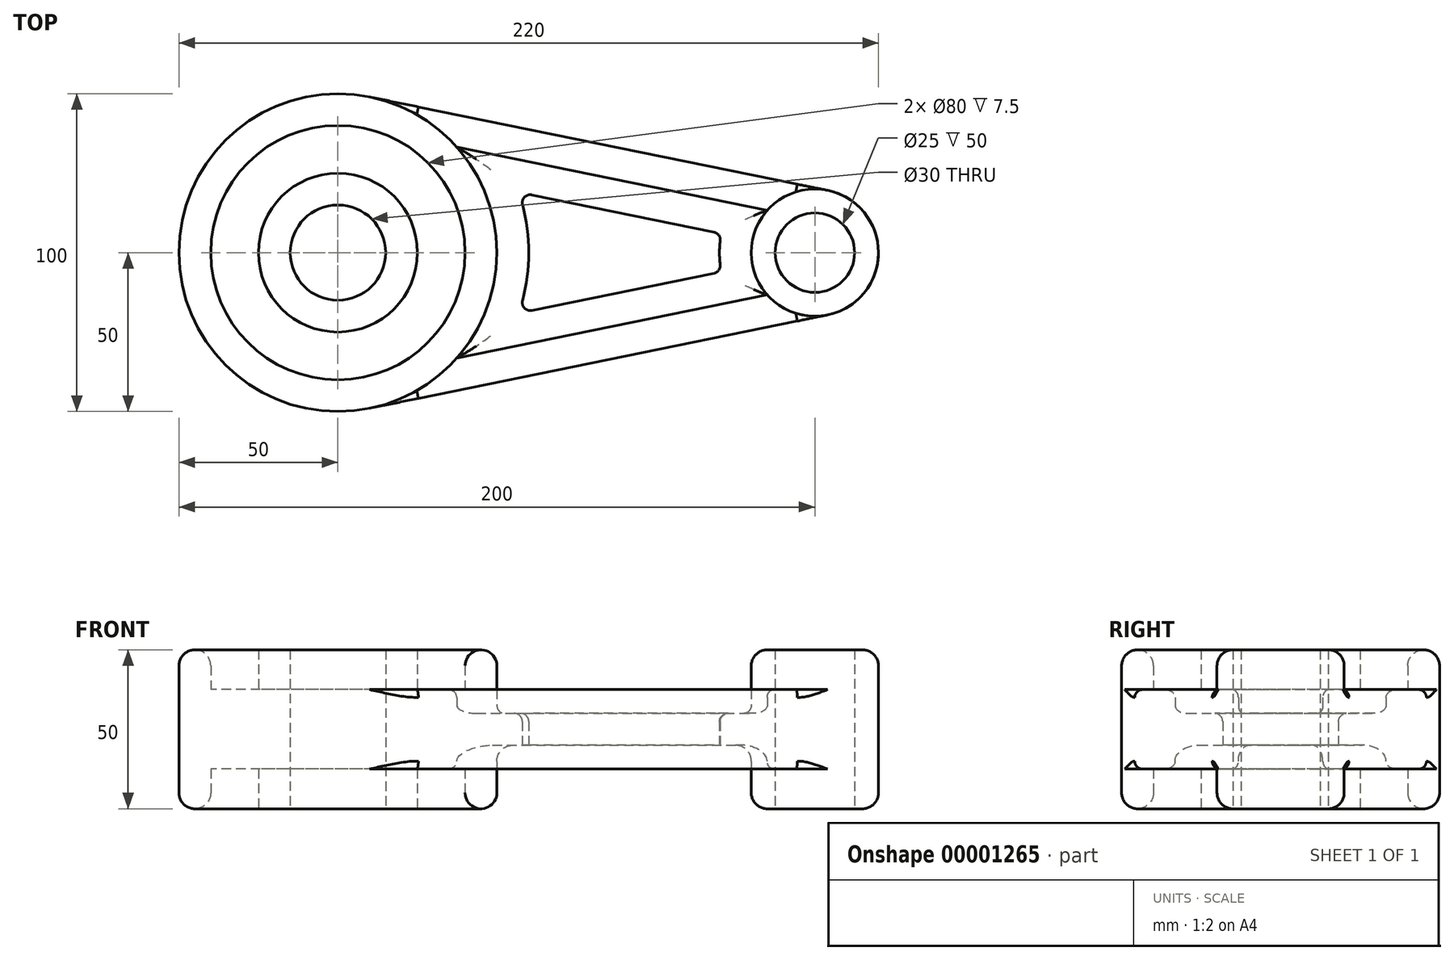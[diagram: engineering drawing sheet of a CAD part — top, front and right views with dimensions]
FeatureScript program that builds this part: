
annotation { "Feature Type Name" : "Feature", "Feature Type Description" : "" }
export const myFeature = defineFeature(function(context is Context, id is Id, definition is map)
    precondition{}
    {
        {
            var Q0;
            Q0=qCreatedBy(makeId("Top.planeOp"),FACE);
            var sketch = newSketch(context, id + "F0", { "sketchPlane" : qUnion([Q0])});
            skCircle(sketch, "E0", {"center": v(150, 0) * mm, "radius": 12.5 * mm});
            skCircle(sketch, "E1", {"center": v(150, 0) * mm, "radius": 20 * mm});
            skCircle(sketch, "E2", {"center": v(0, 0) * mm, "radius": 15 * mm});
            skCircle(sketch, "E3", {"center": v(0, 0) * mm, "radius": 50 * mm});
            skLineSegment(sketch, "E4", {"start": v(10, 48.99) * mm, "end": v(154, 19.6) * mm});
            skLineSegment(sketch, "E5", {"start": v(10, -48.99) * mm, "end": v(154, -19.6) * mm});
            skCircle(sketch, "E6", {"center": v(0, 0) * mm, "radius": 25 * mm});
            skCircle(sketch, "E7", {"center": v(0, 0) * mm, "radius": 40 * mm});
            skLineSegment(sketch, "E8.0", {"start": v(37.4, 33.2) * mm, "end": v(135.03, 13.26) * mm});
            skLineSegment(sketch, "E9.0", {"start": v(37.4, -33.2) * mm, "end": v(135.03, -13.26) * mm});
            skLineSegment(sketch, "E10", {"start": v(0, 0) * mm, "end": v(150, 0) * mm, "construction": true});
            skSolve(sketch);
        }
        {
            var Q0;
            Q0=makeQuery(id+"F0.imprint","IMPRINT",FACE,{"disambiguationData":[TD([[makeQuery(id+"F0.imprint","IMPRINT",EDGE,{"derivedFrom":sQuery(id+"F0.wireOp",EDGE,"E2")}),-1.0]])]});
            var Q1;
            Q1=makeQuery(id+"F0.imprint","IMPRINT",FACE,{"disambiguationData":[TD([[makeQuery(id+"F0.imprint","IMPRINT",EDGE,{"derivedFrom":sQuery(id+"F0.wireOp",EDGE,"E7")}),-1.0]])]});
            var Q2;
            Q2=makeQuery(id+"F0.imprint","IMPRINT",FACE,{"disambiguationData":[TD([[makeQuery(id+"F0.imprint","IMPRINT",EDGE,{"derivedFrom":sQuery(id+"F0.wireOp",EDGE,"E0")}),-1.0]])]});
            extrude(context, id + "F1", {"entities" : qUnion([Q0, Q1, Q2]), "depth" : 50 * mm, "symmetric" : true});
        }
        {
            var Q0;
            Q0=makeQuery(id+"F0.imprint","IMPRINT",FACE,{"disambiguationData":[TD([[makeQuery(id+"F0.imprint","IMPRINT",EDGE,{"derivedFrom":sQuery(id+"F0.wireOp",EDGE,"E6")}),-1.0]])]});
            var Q1;
            {var subQ0=sQuery(id+"F0.wireOp",EDGE,"E4");Q1=makeQuery(id+"F0.imprint","IMPRINT",FACE,{"disambiguationData":[TD([[makeQuery(id+"F0.imprint","IMPRINT",EDGE,{"derivedFrom":subQ0}),-1.0]])]});}
            var Q2;
            {var subQ0=sQuery(id+"F0.wireOp",EDGE,"E5");Q2=makeQuery(id+"F0.imprint","IMPRINT",FACE,{"disambiguationData":[TD([[makeQuery(id+"F0.imprint","IMPRINT",EDGE,{"derivedFrom":subQ0}),1.0]])]});}
            extrude(context, id + "F2", {"entities" : qUnion([Q0, Q1, Q2]), "operationType" : NewBodyOperationType.ADD, "depth" : 25 * mm, "symmetric" : true});
        }
        {
            var Q0;
            {var subQ0=sQuery(id+"F0.wireOp",EDGE,"E8.0");Q0=makeQuery(id+"F0.imprint","IMPRINT",FACE,{"disambiguationData":[TD([[makeQuery(id+"F0.imprint","IMPRINT",EDGE,{"derivedFrom":subQ0}),-1.0]])]});}
            extrude(context, id + "F3", {"entities" : qUnion([Q0]), "operationType" : NewBodyOperationType.ADD, "depth" : 10 * mm, "symmetric" : true});
        }
        {
            var Q0;
            Q0=makeQuery(id+"F2.opExtrude","CAP_EDGE",EDGE,{"disambiguationData":[OSD([sQuery(id+"F0.wireOp",EDGE,"E3")])],"isStart":false});
            var Q1;
            Q1=makeQuery(id+"F2.opExtrude","CAP_EDGE",EDGE,{"disambiguationData":[OSD([sQuery(id+"F0.wireOp",EDGE,"E6")])],"isStart":false});
            var Q2;
            Q2=makeQuery(id+"F2.opExtrude","CAP_EDGE",EDGE,{"disambiguationData":[OSD([sQuery(id+"F0.wireOp",EDGE,"E7")])],"isStart":false});
            var Q3;
            Q3=makeQuery(id+"F2.opExtrude","CAP_EDGE",EDGE,{"disambiguationData":[OSD([sQuery(id+"F0.wireOp",EDGE,"E3")])],"isStart":true});
            var Q4;
            Q4=makeQuery(id+"F2.opExtrude","CAP_EDGE",EDGE,{"disambiguationData":[OSD([sQuery(id+"F0.wireOp",EDGE,"E7")])],"isStart":true});
            var Q5;
            Q5=makeQuery(id+"F2.opExtrude","CAP_EDGE",EDGE,{"disambiguationData":[OSD([sQuery(id+"F0.wireOp",EDGE,"E6")])],"isStart":true});
            var Q6;
            Q6=makeQuery(id+"F2.opExtrude","CAP_EDGE",EDGE,{"disambiguationData":[OSD([sQuery(id+"F0.wireOp",EDGE,"E1")])],"isStart":true});
            var Q7;
            Q7=makeQuery(id+"F2.opExtrude","CAP_EDGE",EDGE,{"disambiguationData":[OSD([sQuery(id+"F0.wireOp",EDGE,"E1")])],"isStart":false});
            var Q8;
            Q8=makeQuery(id+"F3.opExtrude","CAP_EDGE",EDGE,{"disambiguationData":[OSD([sQuery(id+"F0.wireOp",EDGE,"E8.0")])],"isStart":false});
            var Q9;
            Q9=makeQuery(id+"F3.opExtrude","CAP_EDGE",EDGE,{"disambiguationData":[OSD([sQuery(id+"F0.wireOp",EDGE,"E3")])],"isStart":false});
            var Q10;
            Q10=makeQuery(id+"F3.opExtrude","CAP_EDGE",EDGE,{"disambiguationData":[OSD([sQuery(id+"F0.wireOp",EDGE,"E9.0")])],"isStart":false});
            var Q11;
            Q11=makeQuery(id+"F3.opExtrude","CAP_EDGE",EDGE,{"disambiguationData":[OSD([sQuery(id+"F0.wireOp",EDGE,"E1")])],"isStart":false});
            var Q12;
            {var subQ0=sQuery(id+"F0.wireOp",EDGE,"E1");var subQ1=sQuery(id+"F0.wireOp",EDGE,"E8.0");var subQ2=sQuery(id+"F0.wireOp",EDGE,"E3");Q12=makeQuery(id+"F3.boolean.opBoolean","SPLIT",EDGE,{"disambiguationData":[TD([makeQuery(id+"F2.opExtrude","CAP_FACE",FACE,{"disambiguationData":[OSD([subQ0,subQ2,sQuery(id+"F0.wireOp",EDGE,"E4"),subQ1])],"isStart":false})])],"derivedFrom":makeQuery(id+"F2.opExtrude","SWEPT_EDGE",EDGE,{"disambiguationData":[OSD([subQ0,subQ1])]})});}
            var Q13;
            {var subQ0=sQuery(id+"F0.wireOp",EDGE,"E1");var subQ1=sQuery(id+"F0.wireOp",EDGE,"E9.0");var subQ2=sQuery(id+"F0.wireOp",EDGE,"E3");Q13=makeQuery(id+"F3.boolean.opBoolean","SPLIT",EDGE,{"disambiguationData":[TD([makeQuery(id+"F2.opExtrude","CAP_FACE",FACE,{"disambiguationData":[OSD([subQ0,subQ2,sQuery(id+"F0.wireOp",EDGE,"E5"),subQ1])],"isStart":false})])],"derivedFrom":makeQuery(id+"F2.opExtrude","SWEPT_EDGE",EDGE,{"disambiguationData":[OSD([subQ0,subQ1])]})});}
            var Q14;
            Q14=makeQuery(id+"F3.opExtrude","CAP_EDGE",EDGE,{"disambiguationData":[OSD([sQuery(id+"F0.wireOp",EDGE,"E3")])],"isStart":true});
            var Q15;
            Q15=makeQuery(id+"F3.opExtrude","CAP_EDGE",EDGE,{"disambiguationData":[OSD([sQuery(id+"F0.wireOp",EDGE,"E9.0")])],"isStart":true});
            var Q16;
            Q16=makeQuery(id+"F3.opExtrude","CAP_EDGE",EDGE,{"disambiguationData":[OSD([sQuery(id+"F0.wireOp",EDGE,"E8.0")])],"isStart":true});
            var Q17;
            Q17=makeQuery(id+"F3.opExtrude","CAP_FACE",FACE,{"disambiguationData":[OSD([sQuery(id+"F0.wireOp",EDGE,"E1"),sQuery(id+"F0.wireOp",EDGE,"E3"),sQuery(id+"F0.wireOp",EDGE,"E8.0"),sQuery(id+"F0.wireOp",EDGE,"E9.0")])],"isStart":true});
            var Q18;
            {var subQ0=sQuery(id+"F0.wireOp",EDGE,"E1");var subQ1=sQuery(id+"F0.wireOp",EDGE,"E8.0");var subQ2=sQuery(id+"F0.wireOp",EDGE,"E3");Q18=makeQuery(id+"F3.boolean.opBoolean","SPLIT",EDGE,{"disambiguationData":[TD([makeQuery(id+"F2.opExtrude","CAP_FACE",FACE,{"disambiguationData":[OSD([subQ0,subQ2,sQuery(id+"F0.wireOp",EDGE,"E4"),subQ1])],"isStart":true})])],"derivedFrom":makeQuery(id+"F2.opExtrude","SWEPT_EDGE",EDGE,{"disambiguationData":[OSD([subQ0,subQ1])]})});}
            var Q19;
            {var subQ0=sQuery(id+"F0.wireOp",EDGE,"E1");var subQ1=sQuery(id+"F0.wireOp",EDGE,"E9.0");var subQ2=sQuery(id+"F0.wireOp",EDGE,"E3");Q19=makeQuery(id+"F3.boolean.opBoolean","SPLIT",EDGE,{"disambiguationData":[TD([makeQuery(id+"F2.opExtrude","CAP_FACE",FACE,{"disambiguationData":[OSD([subQ0,subQ2,sQuery(id+"F0.wireOp",EDGE,"E5"),subQ1])],"isStart":true})])],"derivedFrom":makeQuery(id+"F2.opExtrude","SWEPT_EDGE",EDGE,{"disambiguationData":[OSD([subQ0,subQ1])]})});}
            var Q20;
            Q20=makeQuery(id+"F1.opExtrude","CAP_EDGE",EDGE,{"disambiguationData":[OSD([sQuery(id+"F0.wireOp",EDGE,"E1")])],"isStart":true});
            var Q21;
            Q21=makeQuery(id+"F1.opExtrude","CAP_EDGE",EDGE,{"disambiguationData":[OSD([sQuery(id+"F0.wireOp",EDGE,"E1")])],"isStart":false});
            var Q22;
            Q22=makeQuery(id+"F1.opExtrude","CAP_EDGE",EDGE,{"disambiguationData":[OSD([sQuery(id+"F0.wireOp",EDGE,"E3")])],"isStart":true});
            var Q23;
            Q23=makeQuery(id+"F1.opExtrude","CAP_EDGE",EDGE,{"disambiguationData":[OSD([sQuery(id+"F0.wireOp",EDGE,"E3")])],"isStart":false});
            var Q24;
            {var subQ0=sQuery(id+"F0.wireOp",EDGE,"E3");var subQ1=sQuery(id+"F0.wireOp",EDGE,"E8.0");var subQ2=sQuery(id+"F0.wireOp",EDGE,"E1");Q24=makeQuery(id+"F3.boolean.opBoolean","SPLIT",EDGE,{"disambiguationData":[TD([makeQuery(id+"F2.opExtrude","CAP_FACE",FACE,{"disambiguationData":[OSD([subQ2,subQ0,sQuery(id+"F0.wireOp",EDGE,"E4"),subQ1])],"isStart":false})])],"derivedFrom":makeQuery(id+"F2.opExtrude","SWEPT_EDGE",EDGE,{"disambiguationData":[OSD([subQ0,subQ1])]})});}
            var Q25;
            {var subQ0=sQuery(id+"F0.wireOp",EDGE,"E3");var subQ1=sQuery(id+"F0.wireOp",EDGE,"E9.0");var subQ2=sQuery(id+"F0.wireOp",EDGE,"E1");Q25=makeQuery(id+"F3.boolean.opBoolean","SPLIT",EDGE,{"disambiguationData":[TD([makeQuery(id+"F2.opExtrude","CAP_FACE",FACE,{"disambiguationData":[OSD([subQ2,subQ0,sQuery(id+"F0.wireOp",EDGE,"E5"),subQ1])],"isStart":false})])],"derivedFrom":makeQuery(id+"F2.opExtrude","SWEPT_EDGE",EDGE,{"disambiguationData":[OSD([subQ0,subQ1])]})});}
            var Q26;
            {var subQ0=sQuery(id+"F0.wireOp",EDGE,"E3");var subQ1=sQuery(id+"F0.wireOp",EDGE,"E8.0");var subQ2=sQuery(id+"F0.wireOp",EDGE,"E1");Q26=makeQuery(id+"F3.boolean.opBoolean","SPLIT",EDGE,{"disambiguationData":[TD([makeQuery(id+"F2.opExtrude","CAP_FACE",FACE,{"disambiguationData":[OSD([subQ2,subQ0,sQuery(id+"F0.wireOp",EDGE,"E4"),subQ1])],"isStart":true})])],"derivedFrom":makeQuery(id+"F2.opExtrude","SWEPT_EDGE",EDGE,{"disambiguationData":[OSD([subQ0,subQ1])]})});}
            var Q27;
            {var subQ0=sQuery(id+"F0.wireOp",EDGE,"E3");var subQ1=sQuery(id+"F0.wireOp",EDGE,"E9.0");var subQ2=sQuery(id+"F0.wireOp",EDGE,"E1");Q27=makeQuery(id+"F3.boolean.opBoolean","SPLIT",EDGE,{"disambiguationData":[TD([makeQuery(id+"F2.opExtrude","CAP_FACE",FACE,{"disambiguationData":[OSD([subQ2,subQ0,sQuery(id+"F0.wireOp",EDGE,"E5"),subQ1])],"isStart":true})])],"derivedFrom":makeQuery(id+"F2.opExtrude","SWEPT_EDGE",EDGE,{"disambiguationData":[OSD([subQ0,subQ1])]})});}
            var Q28;
            Q28=makeQuery(id+"F1.opExtrude","CAP_FACE",FACE,{"disambiguationData":[OSD([sQuery(id+"F0.wireOp",EDGE,"E3"),sQuery(id+"F0.wireOp",EDGE,"E7")])],"isStart":true});
            var Q29;
            Q29=makeQuery(id+"F1.opExtrude","CAP_FACE",FACE,{"disambiguationData":[OSD([sQuery(id+"F0.wireOp",EDGE,"E3"),sQuery(id+"F0.wireOp",EDGE,"E7")])],"isStart":false});
            fillet(context, id + "F4", {"entities" : qUnion([Q0, Q1, Q2, Q3, Q4, Q5, Q6, Q7, Q8, Q9, Q10, Q11, Q12, Q13, Q14, Q15, Q16, Q17, Q18, Q19, Q20, Q21, Q22, Q23, Q24, Q25, Q26, Q27, Q28, Q29]), "radius" : 5 * mm, "tangentPropagation" : true, "allowEdgeOverflow" : false});
        }
        {
            var Q0;
            Q0=makeQuery(id+"F3.opExtrude","CAP_FACE",FACE,{"disambiguationData":[OSD([sQuery(id+"F0.wireOp",EDGE,"E1"),sQuery(id+"F0.wireOp",EDGE,"E3"),sQuery(id+"F0.wireOp",EDGE,"E8.0"),sQuery(id+"F0.wireOp",EDGE,"E9.0")])],"isStart":true});
            var sketch = newSketch(context, id + "F5", { "sketchPlane" : qUnion([Q0])});
            skLineSegment(sketch, "E11.0", {"start": v(120.6, 6) * mm, "end": v(56.91, 19) * mm});
            skArc(sketch, "E11.1", {"start": v(120.6, -6) * mm, "mid": v(120, 0) * mm, "end": v(120.6, 6) * mm});
            skLineSegment(sketch, "E11.2", {"start": v(56.91, -19) * mm, "end": v(120.6, -6) * mm});
            skArc(sketch, "E11.3", {"start": v(56.91, 19) * mm, "mid": v(60, 0) * mm, "end": v(56.91, -19) * mm});
            skSolve(sketch);
        }
        {
            var Q0;
            Q0=makeQuery(id+"F5.imprint","IMPRINT",FACE,{"disambiguationData":[TD([[makeQuery(id+"F5.imprint","IMPRINT",EDGE,{"derivedFrom":sQuery(id+"F5.wireOp",EDGE,"E11.0")}),1.0]])]});
            extrude(context, id + "F6", {"entities" : qUnion([Q0]), "operationType" : NewBodyOperationType.REMOVE, "oppositeDirection" : true, "depth" : 25 * mm});
        }
        {
            var Q0;
            Q0=makeQuery(id+"F6.boolean.opBoolean","COPY",EDGE,{"derivedFrom":makeQuery(id+"F6.opExtrude","CAP_EDGE",EDGE,{"disambiguationData":[OSD([sQuery(id+"F5.wireOp",EDGE,"E11.0")])],"isStart":true})});
            var Q1;
            Q1=makeQuery(id+"F6.boolean.opBoolean","COPY",EDGE,{"derivedFrom":makeQuery(id+"F6.opExtrude","CAP_EDGE",EDGE,{"disambiguationData":[OSD([sQuery(id+"F5.wireOp",EDGE,"E11.1")])],"isStart":true})});
            var Q2;
            Q2=makeQuery(id+"F6.boolean.opBoolean","COPY",EDGE,{"derivedFrom":makeQuery(id+"F6.opExtrude","CAP_EDGE",EDGE,{"disambiguationData":[OSD([sQuery(id+"F5.wireOp",EDGE,"E11.2")])],"isStart":true})});
            var Q3;
            Q3=makeQuery(id+"F6.boolean.opBoolean","COPY",EDGE,{"derivedFrom":makeQuery(id+"F6.opExtrude","CAP_EDGE",EDGE,{"disambiguationData":[OSD([sQuery(id+"F5.wireOp",EDGE,"E11.3")])],"isStart":true})});
            var Q4;
            Q4=makeQuery(id+"F6.boolean.opBoolean","INTERSECT",EDGE,{"derivedFrom":[makeQuery(id+"F3.opExtrude","CAP_FACE",FACE,{"disambiguationData":[OSD([sQuery(id+"F0.wireOp",EDGE,"E1"),sQuery(id+"F0.wireOp",EDGE,"E3"),sQuery(id+"F0.wireOp",EDGE,"E8.0"),sQuery(id+"F0.wireOp",EDGE,"E9.0")])],"isStart":false}),makeQuery(id+"F6.opExtrude","SWEPT_FACE",FACE,{"disambiguationData":[OSD([sQuery(id+"F5.wireOp",EDGE,"E11.1")])]})]});
            var Q5;
            Q5=makeQuery(id+"F6.boolean.opBoolean","INTERSECT",EDGE,{"derivedFrom":[makeQuery(id+"F3.opExtrude","CAP_FACE",FACE,{"disambiguationData":[OSD([sQuery(id+"F0.wireOp",EDGE,"E1"),sQuery(id+"F0.wireOp",EDGE,"E3"),sQuery(id+"F0.wireOp",EDGE,"E8.0"),sQuery(id+"F0.wireOp",EDGE,"E9.0")])],"isStart":false}),makeQuery(id+"F6.opExtrude","SWEPT_FACE",FACE,{"disambiguationData":[OSD([sQuery(id+"F5.wireOp",EDGE,"E11.2")])]})]});
            var Q6;
            Q6=makeQuery(id+"F3.opExtrude","CAP_FACE",FACE,{"disambiguationData":[OSD([sQuery(id+"F0.wireOp",EDGE,"E1"),sQuery(id+"F0.wireOp",EDGE,"E3"),sQuery(id+"F0.wireOp",EDGE,"E8.0"),sQuery(id+"F0.wireOp",EDGE,"E9.0")])],"isStart":false});
            var Q7;
            Q7=makeQuery(id+"F6.boolean.opBoolean","INTERSECT",EDGE,{"derivedFrom":[makeQuery(id+"F3.opExtrude","CAP_FACE",FACE,{"disambiguationData":[OSD([sQuery(id+"F0.wireOp",EDGE,"E1"),sQuery(id+"F0.wireOp",EDGE,"E3"),sQuery(id+"F0.wireOp",EDGE,"E8.0"),sQuery(id+"F0.wireOp",EDGE,"E9.0")])],"isStart":false}),makeQuery(id+"F6.opExtrude","SWEPT_FACE",FACE,{"disambiguationData":[OSD([sQuery(id+"F5.wireOp",EDGE,"E11.0")])]})]});
            var Q8;
            Q8=makeQuery(id+"F2.opExtrude","CAP_EDGE",EDGE,{"disambiguationData":[OSD([sQuery(id+"F0.wireOp",EDGE,"E5")])],"isStart":true});
            var Q9;
            Q9=makeQuery(id+"F2.opExtrude","CAP_EDGE",EDGE,{"disambiguationData":[OSD([sQuery(id+"F0.wireOp",EDGE,"E5")])],"isStart":false});
            var Q10;
            Q10=makeQuery(id+"F2.opExtrude","CAP_EDGE",EDGE,{"disambiguationData":[OSD([sQuery(id+"F0.wireOp",EDGE,"E9.0")])],"isStart":false});
            var Q11;
            Q11=makeQuery(id+"F2.opExtrude","CAP_EDGE",EDGE,{"disambiguationData":[OSD([sQuery(id+"F0.wireOp",EDGE,"E8.0")])],"isStart":false});
            var Q12;
            Q12=makeQuery(id+"F2.opExtrude","CAP_EDGE",EDGE,{"disambiguationData":[OSD([sQuery(id+"F0.wireOp",EDGE,"E4")])],"isStart":false});
            var Q13;
            Q13=makeQuery(id+"F2.opExtrude","CAP_EDGE",EDGE,{"disambiguationData":[OSD([sQuery(id+"F0.wireOp",EDGE,"E4")])],"isStart":true});
            var Q14;
            Q14=makeQuery(id+"F2.opExtrude","CAP_EDGE",EDGE,{"disambiguationData":[OSD([sQuery(id+"F0.wireOp",EDGE,"E8.0")])],"isStart":true});
            var Q15;
            Q15=makeQuery(id+"F2.opExtrude","CAP_EDGE",EDGE,{"disambiguationData":[OSD([sQuery(id+"F0.wireOp",EDGE,"E9.0")])],"isStart":true});
            var Q16;
            Q16=makeQuery(id+"F6.boolean.opBoolean","COPY",EDGE,{"derivedFrom":makeQuery(id+"F6.opExtrude","SWEPT_EDGE",EDGE,{"disambiguationData":[OSD([sQuery(id+"F5.wireOp",EDGE,"E11.0"),sQuery(id+"F5.wireOp",EDGE,"E11.3")])]})});
            var Q17;
            Q17=makeQuery(id+"F6.boolean.opBoolean","COPY",EDGE,{"derivedFrom":makeQuery(id+"F6.opExtrude","SWEPT_EDGE",EDGE,{"disambiguationData":[OSD([sQuery(id+"F5.wireOp",EDGE,"E11.2"),sQuery(id+"F5.wireOp",EDGE,"E11.3")])]})});
            var Q18;
            Q18=makeQuery(id+"F6.boolean.opBoolean","COPY",EDGE,{"derivedFrom":makeQuery(id+"F6.opExtrude","SWEPT_EDGE",EDGE,{"disambiguationData":[OSD([sQuery(id+"F5.wireOp",EDGE,"E11.1"),sQuery(id+"F5.wireOp",EDGE,"E11.2")])]})});
            var Q19;
            Q19=makeQuery(id+"F6.boolean.opBoolean","COPY",EDGE,{"derivedFrom":makeQuery(id+"F6.opExtrude","SWEPT_EDGE",EDGE,{"disambiguationData":[OSD([sQuery(id+"F5.wireOp",EDGE,"E11.0"),sQuery(id+"F5.wireOp",EDGE,"E11.1")])]})});
            fillet(context, id + "F7", {"entities" : qUnion([Q0, Q1, Q2, Q3, Q4, Q5, Q6, Q7, Q8, Q9, Q10, Q11, Q12, Q13, Q14, Q15, Q16, Q17, Q18, Q19]), "radius" : 2.5 * mm, "tangentPropagation" : true, "allowEdgeOverflow" : false});
        }
    });
